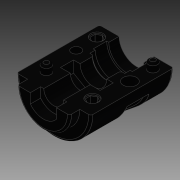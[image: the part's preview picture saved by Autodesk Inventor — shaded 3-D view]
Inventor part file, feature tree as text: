
AUTODESK INVENTOR PART (.ipt)
format: ipt  version: 2014 SP1 (Build 180222100, 222)  size: 251,904 bytes
history: native  units: in
note: dims shown in document units (in); Inventor stores cm internally (conversion verified against a paired STEP export)
features: fillet x1, other x1, imported_body x1
ambient origin geometry x8: Origin, YZ Plane, XZ Plane, XY Plane, X Axis, Y Axis, Z Axis, Center Point
bodies: Body1 (feature_tree)
feature tree (3):
  fillet  "Fillet1"  [1 undecoded]
  other  "217-2428-032 Rev1.ipt1"
  imported_body  "Base1"
note: 1 required parameter value undecoded (feature->parameter linkage not recoverable at this tier; creation-order binding heuristic only, values carry confidence <= 0.55)
